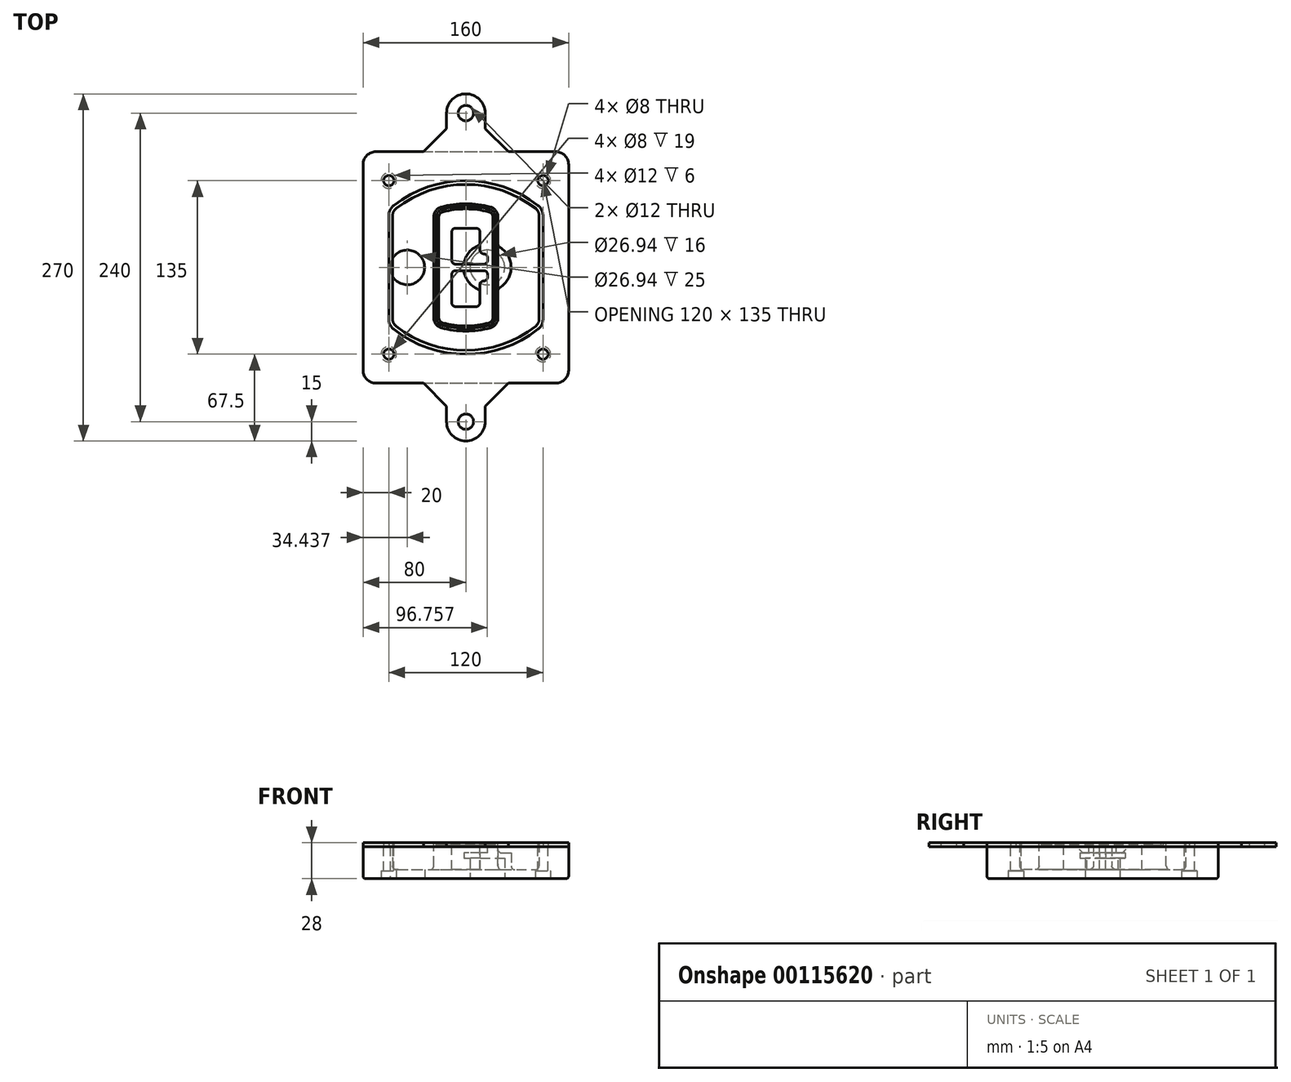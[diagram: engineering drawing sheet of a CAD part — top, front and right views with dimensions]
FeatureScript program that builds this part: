
annotation { "Feature Type Name" : "Feature", "Feature Type Description" : "" }
export const myFeature = defineFeature(function(context is Context, id is Id, definition is map)
    precondition{}
    {
        {
            var Q0;
            Q0=qCreatedBy(makeId("Top.planeOp"),FACE);
            var sketch = newSketch(context, id + "F0", { "sketchPlane" : qUnion([Q0])});
            skPoint(sketch, "E0.rect.middle", {"position": v(0, 0) * mm});
            skLineSegment(sketch, "E1.bottom", {"start": v(-70, -90) * mm, "end": v(70, -90) * mm});
            skLineSegment(sketch, "E1.top", {"start": v(-70, 90) * mm, "end": v(70, 90) * mm});
            skLineSegment(sketch, "E1.left", {"start": v(-80, -80) * mm, "end": v(-80, 80) * mm});
            skLineSegment(sketch, "E1.right", {"start": v(80, -80) * mm, "end": v(80, 80) * mm});
            skLineSegment(sketch, "E2", {"start": v(-80, 90) * mm, "end": v(80, -90) * mm, "construction": true});
            skLineSegment(sketch, "E3", {"start": v(80, 90) * mm, "end": v(-80, -90) * mm, "construction": true});
            skCircle(sketch, "E4", {"center": v(-60, 67.5) * mm, "radius": 4 * mm});
            skCircle(sketch, "E5", {"center": v(60, 67.5) * mm, "radius": 4 * mm});
            skCircle(sketch, "E6", {"center": v(60, -67.5) * mm, "radius": 4 * mm});
            skCircle(sketch, "E7", {"center": v(-60, -67.5) * mm, "radius": 4 * mm});
            skLineSegment(sketch, "E8", {"start": v(-60, 67.5) * mm, "end": v(60, 67.5) * mm, "construction": true});
            skLineSegment(sketch, "E9", {"start": v(60, 67.5) * mm, "end": v(60, -67.5) * mm, "construction": true});
            skLineSegment(sketch, "E10", {"start": v(60, -67.5) * mm, "end": v(-60, -67.5) * mm, "construction": true});
            skLineSegment(sketch, "E11", {"start": v(-60, -67.5) * mm, "end": v(-60, 67.5) * mm, "construction": true});
            skLineSegment(sketch, "E12", {"start": v(-60, 40.3) * mm, "end": v(-60, -40.3) * mm});
            skLineSegment(sketch, "E13", {"start": v(60, 40.3) * mm, "end": v(60, -40.3) * mm});
            skArc(sketch, "E14", {"start": v(56.15, 48.18) * mm, "mid": v(0, 67.5) * mm, "end": v(-56.15, 48.18) * mm});
            skArc(sketch, "E15", {"start": v(-56.15, -48.18) * mm, "mid": v(0, -67.5) * mm, "end": v(56.15, -48.18) * mm});
            skLineSegment(sketch, "E16", {"start": v(-60, 0) * mm, "end": v(60, 0) * mm, "construction": true});
            skPoint(sketch, "E17.visualSharp", {"position": v(-60, -45) * mm});
            skArc(sketch, "E17.filletArc", {"start": v(-60, -40.3) * mm, "mid": v(-58.99, -44.68) * mm, "end": v(-56.15, -48.18) * mm});
            skPoint(sketch, "E18.visualSharp", {"position": v(-60, 45) * mm});
            skArc(sketch, "E18.filletArc", {"start": v(-56.15, 48.18) * mm, "mid": v(-58.99, 44.68) * mm, "end": v(-60, 40.3) * mm});
            skPoint(sketch, "E19.visualSharp", {"position": v(60, 45) * mm});
            skArc(sketch, "E19.filletArc", {"start": v(60, 40.3) * mm, "mid": v(58.99, 44.68) * mm, "end": v(56.15, 48.18) * mm});
            skPoint(sketch, "E20.visualSharp", {"position": v(60, -45) * mm});
            skArc(sketch, "E20.filletArc", {"start": v(56.15, -48.18) * mm, "mid": v(58.99, -44.68) * mm, "end": v(60, -40.3) * mm});
            skPoint(sketch, "E21.visualSharp", {"position": v(-80, 90) * mm});
            skArc(sketch, "E21.filletArc", {"start": v(-70, 90) * mm, "mid": v(-77.07, 87.07) * mm, "end": v(-80, 80) * mm});
            skPoint(sketch, "E22.visualSharp", {"position": v(80, 90) * mm});
            skArc(sketch, "E22.filletArc", {"start": v(80, 80) * mm, "mid": v(77.07, 87.07) * mm, "end": v(70, 90) * mm});
            skPoint(sketch, "E23.visualSharp", {"position": v(80, -90) * mm});
            skArc(sketch, "E23.filletArc", {"start": v(70, -90) * mm, "mid": v(77.07, -87.07) * mm, "end": v(80, -80) * mm});
            skPoint(sketch, "E24.visualSharp", {"position": v(-80, -90) * mm});
            skArc(sketch, "E24.filletArc", {"start": v(-80, -80) * mm, "mid": v(-77.07, -87.07) * mm, "end": v(-70, -90) * mm});
            skArc(sketch, "E25.0", {"start": v(57, 40.3) * mm, "mid": v(56.3, 43.36) * mm, "end": v(54.3, 45.81) * mm});
            skLineSegment(sketch, "E25.1", {"start": v(57, 40.3) * mm, "end": v(57, -40.3) * mm});
            skArc(sketch, "E25.2", {"start": v(54.3, -45.81) * mm, "mid": v(56.3, -43.36) * mm, "end": v(57, -40.3) * mm});
            skArc(sketch, "E25.3", {"start": v(-54.3, -45.81) * mm, "mid": v(0, -64.5) * mm, "end": v(54.3, -45.81) * mm});
            skArc(sketch, "E25.4", {"start": v(-57, -40.3) * mm, "mid": v(-56.3, -43.36) * mm, "end": v(-54.3, -45.81) * mm});
            skArc(sketch, "E25.5", {"start": v(54.3, 45.81) * mm, "mid": v(0, 64.5) * mm, "end": v(-54.3, 45.81) * mm});
            skLineSegment(sketch, "E25.6", {"start": v(-57, 40.3) * mm, "end": v(-57, -40.3) * mm});
            skArc(sketch, "E25.7", {"start": v(-54.3, 45.81) * mm, "mid": v(-56.3, 43.36) * mm, "end": v(-57, 40.3) * mm});
            skArc(sketch, "E26.0", {"start": v(-58.62, 51.33) * mm, "mid": v(-62.58, 46.43) * mm, "end": v(-64, 40.3) * mm});
            skArc(sketch, "E26.1", {"start": v(58.62, 51.33) * mm, "mid": v(0, 71.5) * mm, "end": v(-58.62, 51.33) * mm});
            skArc(sketch, "E26.2", {"start": v(64, 40.3) * mm, "mid": v(62.58, 46.43) * mm, "end": v(58.62, 51.33) * mm});
            skLineSegment(sketch, "E26.3", {"start": v(64, 40.3) * mm, "end": v(64, -40.3) * mm});
            skArc(sketch, "E26.4", {"start": v(58.62, -51.33) * mm, "mid": v(62.58, -46.43) * mm, "end": v(64, -40.3) * mm});
            skLineSegment(sketch, "E26.5", {"start": v(-64, 40.3) * mm, "end": v(-64, -40.3) * mm});
            skArc(sketch, "E26.6", {"start": v(-58.62, -51.33) * mm, "mid": v(0, -71.5) * mm, "end": v(58.62, -51.33) * mm});
            skArc(sketch, "E26.7", {"start": v(-64, -40.3) * mm, "mid": v(-62.58, -46.43) * mm, "end": v(-58.62, -51.33) * mm});
            skSolve(sketch);
        }
        {
            var Q0;
            Q0=makeQuery(id+"F0.imprint","IMPRINT",FACE,{"disambiguationData":[TD([[makeQuery(id+"F0.imprint","IMPRINT",EDGE,{"derivedFrom":sQuery(id+"F0.wireOp",EDGE,"E1.bottom")}),1.0]])]});
            var Q1;
            Q1=makeQuery(id+"F0.imprint","IMPRINT",FACE,{"disambiguationData":[TD([[makeQuery(id+"F0.imprint","IMPRINT",EDGE,{"derivedFrom":sQuery(id+"F0.wireOp",EDGE,"E12")}),1.0]])]});
            var Q2;
            Q2=makeQuery(id+"F0.imprint","IMPRINT",FACE,{"disambiguationData":[TD([[makeQuery(id+"F0.imprint","IMPRINT",EDGE,{"derivedFrom":sQuery(id+"F0.wireOp",EDGE,"E25.0")}),1.0]])]});
            var Q3;
            Q3=makeQuery(id+"F0.imprint","IMPRINT",FACE,{"disambiguationData":[TD([[makeQuery(id+"F0.imprint","IMPRINT",EDGE,{"derivedFrom":sQuery(id+"F0.wireOp",EDGE,"E12")}),-1.0]])]});
            extrude(context, id + "F1", {"entities" : qUnion([Q0, Q1, Q2, Q3]), "oppositeDirection" : true, "depth" : 25 * mm});
        }
        {
            var Q0;
            Q0=makeQuery(id+"F0.imprint","IMPRINT",FACE,{"disambiguationData":[TD([[makeQuery(id+"F0.imprint","IMPRINT",EDGE,{"derivedFrom":sQuery(id+"F0.wireOp",EDGE,"E12")}),1.0]])]});
            extrude(context, id + "F2", {"entities" : qUnion([Q0]), "operationType" : NewBodyOperationType.ADD, "depth" : 3 * mm});
        }
        {
            var Q0;
            Q0=makeQuery(id+"F0.imprint","IMPRINT",FACE,{"disambiguationData":[TD([[makeQuery(id+"F0.imprint","IMPRINT",EDGE,{"derivedFrom":sQuery(id+"F0.wireOp",EDGE,"E25.0")}),1.0]])]});
            extrude(context, id + "F3", {"entities" : qUnion([Q0]), "operationType" : NewBodyOperationType.REMOVE, "oppositeDirection" : true, "depth" : 18 * mm});
        }
        {
            var Q0;
            Q0=makeQuery(id+"F2.opExtrude","CAP_FACE",FACE,{"disambiguationData":[OSD([sQuery(id+"F0.wireOp",EDGE,"E12"),sQuery(id+"F0.wireOp",EDGE,"E13"),sQuery(id+"F0.wireOp",EDGE,"E14"),sQuery(id+"F0.wireOp",EDGE,"E15"),sQuery(id+"F0.wireOp",EDGE,"E17.filletArc"),sQuery(id+"F0.wireOp",EDGE,"E18.filletArc"),sQuery(id+"F0.wireOp",EDGE,"E19.filletArc"),sQuery(id+"F0.wireOp",EDGE,"E20.filletArc"),sQuery(id+"F0.wireOp",EDGE,"E25.0"),sQuery(id+"F0.wireOp",EDGE,"E25.1"),sQuery(id+"F0.wireOp",EDGE,"E25.2"),sQuery(id+"F0.wireOp",EDGE,"E25.3"),sQuery(id+"F0.wireOp",EDGE,"E25.4"),sQuery(id+"F0.wireOp",EDGE,"E25.5"),sQuery(id+"F0.wireOp",EDGE,"E25.6"),sQuery(id+"F0.wireOp",EDGE,"E25.7")])],"isStart":false});
            var sketch = newSketch(context, id + "F4", { "sketchPlane" : qUnion([Q0])});
            skArc(sketch, "E27.0", {"start": v(-19.08, -46.97) * mm, "mid": v(0, -49.5) * mm, "end": v(19.08, -46.97) * mm});
            skArc(sketch, "E28.0", {"start": v(19.08, 46.97) * mm, "mid": v(0, 49.5) * mm, "end": v(-19.08, 46.97) * mm});
            skLineSegment(sketch, "E29", {"start": v(-25, 39.25) * mm, "end": v(-25, -39.25) * mm});
            skLineSegment(sketch, "E30", {"start": v(25, 39.25) * mm, "end": v(25, -39.25) * mm});
            skLineSegment(sketch, "E31", {"start": v(-25, 45.1) * mm, "end": v(25, 45.1) * mm, "construction": true});
            skLineSegment(sketch, "E32", {"start": v(-25, -45.1) * mm, "end": v(25, -45.1) * mm, "construction": true});
            skPoint(sketch, "E33.visualSharp", {"position": v(-25, 45.1) * mm});
            skArc(sketch, "E33.filletArc", {"start": v(-19.08, 46.97) * mm, "mid": v(-23.35, 44.11) * mm, "end": v(-25, 39.25) * mm});
            skPoint(sketch, "E34.visualSharp", {"position": v(25, 45.1) * mm});
            skArc(sketch, "E34.filletArc", {"start": v(25, 39.25) * mm, "mid": v(23.35, 44.11) * mm, "end": v(19.08, 46.97) * mm});
            skPoint(sketch, "E35.visualSharp", {"position": v(25, -45.1) * mm});
            skArc(sketch, "E35.filletArc", {"start": v(19.08, -46.97) * mm, "mid": v(23.35, -44.11) * mm, "end": v(25, -39.25) * mm});
            skPoint(sketch, "E36.visualSharp", {"position": v(-25, -45.1) * mm});
            skArc(sketch, "E36.filletArc", {"start": v(-25, -39.25) * mm, "mid": v(-23.35, -44.11) * mm, "end": v(-19.08, -46.97) * mm});
            skArc(sketch, "E37.0", {"start": v(54.3, 45.81) * mm, "mid": v(0, 64.5) * mm, "end": v(-54.3, 45.81) * mm});
            skArc(sketch, "E37.1", {"start": v(-54.3, 45.81) * mm, "mid": v(-56.3, 43.36) * mm, "end": v(-57, 40.3) * mm});
            skLineSegment(sketch, "E37.2", {"start": v(-57, 40.3) * mm, "end": v(-57, -40.3) * mm});
            skArc(sketch, "E37.3", {"start": v(-57, -40.3) * mm, "mid": v(-56.3, -43.36) * mm, "end": v(-54.3, -45.81) * mm});
            skArc(sketch, "E37.4", {"start": v(-54.3, -45.81) * mm, "mid": v(0, -64.5) * mm, "end": v(54.3, -45.81) * mm});
            skArc(sketch, "E37.5", {"start": v(54.3, -45.81) * mm, "mid": v(56.3, -43.36) * mm, "end": v(57, -40.3) * mm});
            skLineSegment(sketch, "E37.6", {"start": v(57, 40.3) * mm, "end": v(57, -40.3) * mm});
            skArc(sketch, "E37.7", {"start": v(57, 40.3) * mm, "mid": v(56.3, 43.36) * mm, "end": v(54.3, 45.81) * mm});
            skLineSegment(sketch, "E38.0", {"start": v(23, 39.25) * mm, "end": v(23, -39.25) * mm});
            skArc(sketch, "E38.1", {"start": v(18.56, -45.04) * mm, "mid": v(21.76, -42.9) * mm, "end": v(23, -39.25) * mm});
            skArc(sketch, "E38.2", {"start": v(-18.56, -45.04) * mm, "mid": v(0, -47.5) * mm, "end": v(18.56, -45.04) * mm});
            skArc(sketch, "E38.3", {"start": v(-23, -39.25) * mm, "mid": v(-21.76, -42.9) * mm, "end": v(-18.56, -45.04) * mm});
            skLineSegment(sketch, "E38.4", {"start": v(-23, 39.25) * mm, "end": v(-23, -39.25) * mm});
            skArc(sketch, "E38.5", {"start": v(23, 39.25) * mm, "mid": v(21.76, 42.9) * mm, "end": v(18.56, 45.04) * mm});
            skArc(sketch, "E38.6", {"start": v(-18.56, 45.04) * mm, "mid": v(-21.76, 42.9) * mm, "end": v(-23, 39.25) * mm});
            skArc(sketch, "E38.7", {"start": v(18.56, 45.04) * mm, "mid": v(0, 47.5) * mm, "end": v(-18.56, 45.04) * mm});
            skArc(sketch, "E39.0", {"start": v(21, 39.25) * mm, "mid": v(20.18, 41.68) * mm, "end": v(18.04, 43.1) * mm});
            skLineSegment(sketch, "E39.1", {"start": v(21, 39.25) * mm, "end": v(21, -39.25) * mm});
            skArc(sketch, "E39.2", {"start": v(18.04, -43.1) * mm, "mid": v(20.18, -41.68) * mm, "end": v(21, -39.25) * mm});
            skArc(sketch, "E39.3", {"start": v(-18.04, -43.1) * mm, "mid": v(0, -45.5) * mm, "end": v(18.04, -43.1) * mm});
            skArc(sketch, "E39.4", {"start": v(-21, -39.25) * mm, "mid": v(-20.18, -41.68) * mm, "end": v(-18.04, -43.1) * mm});
            skArc(sketch, "E39.5", {"start": v(18.04, 43.1) * mm, "mid": v(0, 45.5) * mm, "end": v(-18.04, 43.1) * mm});
            skLineSegment(sketch, "E39.6", {"start": v(-21, 39.25) * mm, "end": v(-21, -39.25) * mm});
            skArc(sketch, "E39.7", {"start": v(-18.04, 43.1) * mm, "mid": v(-20.18, 41.68) * mm, "end": v(-21, 39.25) * mm});
            skLineSegment(sketch, "E40", {"start": v(-25, 0) * mm, "end": v(25, 0) * mm, "construction": true});
            skLineSegment(sketch, "E41", {"start": v(-11, 5.5) * mm, "end": v(-11, 27.5) * mm});
            skLineSegment(sketch, "E42", {"start": v(-8, 30.5) * mm, "end": v(8, 30.5) * mm});
            skLineSegment(sketch, "E43", {"start": v(11, 27.5) * mm, "end": v(11, 13.5) * mm});
            skLineSegment(sketch, "E44", {"start": v(14, 10.5) * mm, "end": v(14, 10.5) * mm});
            skLineSegment(sketch, "E45", {"start": v(17, 7.5) * mm, "end": v(17, 5.5) * mm});
            skLineSegment(sketch, "E46", {"start": v(14, 2.5) * mm, "end": v(-8, 2.5) * mm});
            skPoint(sketch, "E47.visualSharp", {"position": v(-11, 30.5) * mm});
            skArc(sketch, "E47.filletArc", {"start": v(-8, 30.5) * mm, "mid": v(-10.12, 29.62) * mm, "end": v(-11, 27.5) * mm});
            skPoint(sketch, "E48.visualSharp", {"position": v(11, 30.5) * mm});
            skArc(sketch, "E48.filletArc", {"start": v(11, 27.5) * mm, "mid": v(10.12, 29.62) * mm, "end": v(8, 30.5) * mm});
            skPoint(sketch, "E49.visualSharp", {"position": v(11, 10.5) * mm});
            skArc(sketch, "E49.filletArc", {"start": v(11, 13.5) * mm, "mid": v(11.88, 11.38) * mm, "end": v(14, 10.5) * mm});
            skPoint(sketch, "E50.visualSharp", {"position": v(17, 10.5) * mm});
            skArc(sketch, "E50.filletArc", {"start": v(17, 7.5) * mm, "mid": v(16.12, 9.62) * mm, "end": v(14, 10.5) * mm});
            skPoint(sketch, "E51.visualSharp", {"position": v(17, 2.5) * mm});
            skArc(sketch, "E51.filletArc", {"start": v(14, 2.5) * mm, "mid": v(16.12, 3.38) * mm, "end": v(17, 5.5) * mm});
            skPoint(sketch, "E52.visualSharp", {"position": v(-11, 2.5) * mm});
            skArc(sketch, "E52.filletArc", {"start": v(-11, 5.5) * mm, "mid": v(-10.12, 3.38) * mm, "end": v(-8, 2.5) * mm});
            skLineSegment(sketch, "E53.0.MirrorCS", {"start": v(14, -2.5) * mm, "end": v(-8, -2.5) * mm});
            skArc(sketch, "E54.0.MirrorCS", {"start": v(-11, -5.5) * mm, "mid": v(-10.12, -3.38) * mm, "end": v(-8, -2.5) * mm});
            skLineSegment(sketch, "E55.0.MirrorCS", {"start": v(-11, -5.5) * mm, "end": v(-11, -27.5) * mm});
            skArc(sketch, "E56.0.MirrorCS", {"start": v(-8, -30.5) * mm, "mid": v(-10.12, -29.62) * mm, "end": v(-11, -27.5) * mm});
            skLineSegment(sketch, "E57.0.MirrorCS", {"start": v(-8, -30.5) * mm, "end": v(8, -30.5) * mm});
            skArc(sketch, "E58.0.MirrorCS", {"start": v(11, -27.5) * mm, "mid": v(10.12, -29.62) * mm, "end": v(8, -30.5) * mm});
            skLineSegment(sketch, "E59.0.MirrorCS", {"start": v(11, -27.5) * mm, "end": v(11, -13.5) * mm});
            skArc(sketch, "E60.0.MirrorCS", {"start": v(11, -13.5) * mm, "mid": v(11.88, -11.38) * mm, "end": v(14, -10.5) * mm});
            skArc(sketch, "E61.0.MirrorCS", {"start": v(17, -7.5) * mm, "mid": v(16.12, -9.62) * mm, "end": v(14, -10.5) * mm});
            skLineSegment(sketch, "E62.0.MirrorCS", {"start": v(17, -7.5) * mm, "end": v(17, -5.5) * mm});
            skArc(sketch, "E63.0.MirrorCS", {"start": v(14, -2.5) * mm, "mid": v(16.12, -3.38) * mm, "end": v(17, -5.5) * mm});
            skSolve(sketch);
        }
        {
            var Q0;
            Q0=makeQuery(id+"F4.imprint","IMPRINT",FACE,{"disambiguationData":[TD([[makeQuery(id+"F4.imprint","IMPRINT",EDGE,{"derivedFrom":sQuery(id+"F4.wireOp",EDGE,"E27.0")}),1.0]])]});
            var Q1;
            Q1=makeQuery(id+"F4.imprint","IMPRINT",FACE,{"disambiguationData":[TD([[makeQuery(id+"F4.imprint","IMPRINT",EDGE,{"derivedFrom":sQuery(id+"F4.wireOp",EDGE,"E38.0")}),-1.0]])]});
            var Q2;
            Q2=makeQuery(id+"F4.imprint","IMPRINT",FACE,{"disambiguationData":[TD([[makeQuery(id+"F4.imprint","IMPRINT",EDGE,{"derivedFrom":sQuery(id+"F4.wireOp",EDGE,"E39.0")}),1.0]])]});
            extrude(context, id + "F5", {"entities" : qUnion([Q0, Q1, Q2]), "operationType" : NewBodyOperationType.ADD, "endBound" : BoundingType.UP_TO_NEXT, "oppositeDirection" : true, "depth" : 25 * mm});
        }
        {
            var Q0;
            Q0=makeQuery(id+"F4.imprint","IMPRINT",FACE,{"disambiguationData":[TD([[makeQuery(id+"F4.imprint","IMPRINT",EDGE,{"derivedFrom":sQuery(id+"F4.wireOp",EDGE,"E38.0")}),-1.0]])]});
            extrude(context, id + "F6", {"entities" : qUnion([Q0]), "operationType" : NewBodyOperationType.REMOVE, "oppositeDirection" : true, "depth" : 2 * mm});
        }
        {
            var Q0;
            Q0=makeQuery(id+"F1.opExtrude","CAP_FACE",FACE,{"disambiguationData":[OSD([sQuery(id+"F0.wireOp",EDGE,"E1.bottom"),sQuery(id+"F0.wireOp",EDGE,"E1.top"),sQuery(id+"F0.wireOp",EDGE,"E1.left"),sQuery(id+"F0.wireOp",EDGE,"E1.right"),sQuery(id+"F0.wireOp",EDGE,"E4"),sQuery(id+"F0.wireOp",EDGE,"E5"),sQuery(id+"F0.wireOp",EDGE,"E6"),sQuery(id+"F0.wireOp",EDGE,"E7"),sQuery(id+"F0.wireOp",EDGE,"E21.filletArc"),sQuery(id+"F0.wireOp",EDGE,"E22.filletArc"),sQuery(id+"F0.wireOp",EDGE,"E23.filletArc"),sQuery(id+"F0.wireOp",EDGE,"E24.filletArc")])],"isStart":false});
            var sketch = newSketch(context, id + "F7", { "sketchPlane" : qUnion([Q0])});
            skCircle(sketch, "E64", {"center": v(16.76, 0) * mm, "radius": 13.47 * mm});
            skCircle(sketch, "E65", {"center": v(-45.56, 0) * mm, "radius": 13.47 * mm});
            skLineSegment(sketch, "E66", {"start": v(80, 0) * mm, "end": v(-80, 0) * mm});
            skCircle(sketch, "E67", {"center": v(16.76, 0) * mm, "radius": 18.47 * mm});
            skCircle(sketch, "E68", {"center": v(60, -67.5) * mm, "radius": 6 * mm});
            skCircle(sketch, "E69", {"center": v(-60, -67.5) * mm, "radius": 6 * mm});
            skCircle(sketch, "E70", {"center": v(-60, 67.5) * mm, "radius": 6 * mm});
            skCircle(sketch, "E71", {"center": v(60, 67.5) * mm, "radius": 6 * mm});
            skSolve(sketch);
        }
        {
            var Q0;
            {var subQ1=sQuery(id+"F7.wireOp",EDGE,"E66");var subQ4=sQuery(id+"F7.wireOp",EDGE,"E64");var subQ6=makeQuery(id+"F7.imprint","INTERSECT",VERTEX,{"disambiguationData":[OD(0.0)],"derivedFrom":[subQ4,subQ1]});Q0=makeQuery(id+"F7.imprint","IMPRINT",FACE,{"disambiguationData":[TD([[makeQuery(id+"F7.imprint","IMPRINT",EDGE,{"disambiguationData":[TD([[subQ6,-1.0]])],"derivedFrom":subQ4}),-1.0]])]});}
            var Q1;
            {var subQ0=sQuery(id+"F7.wireOp",EDGE,"E66");var subQ1=sQuery(id+"F7.wireOp",EDGE,"E64");var subQ3=makeQuery(id+"F7.imprint","INTERSECT",VERTEX,{"disambiguationData":[OD(0.0)],"derivedFrom":[subQ1,subQ0]});Q1=makeQuery(id+"F7.imprint","IMPRINT",FACE,{"disambiguationData":[TD([[makeQuery(id+"F7.imprint","IMPRINT",EDGE,{"disambiguationData":[TD([[subQ3,-1.0]])],"derivedFrom":subQ1}),1.0]])]});}
            var Q2;
            {var subQ0=sQuery(id+"F7.wireOp",EDGE,"E66");var subQ1=sQuery(id+"F7.wireOp",EDGE,"E64");var subQ3=makeQuery(id+"F7.imprint","INTERSECT",VERTEX,{"disambiguationData":[OD(0.0)],"derivedFrom":[subQ1,subQ0]});Q2=makeQuery(id+"F7.imprint","IMPRINT",FACE,{"disambiguationData":[TD([[makeQuery(id+"F7.imprint","IMPRINT",EDGE,{"disambiguationData":[TD([[subQ3,1.0]])],"derivedFrom":subQ1}),1.0]])]});}
            var Q3;
            {var subQ1=sQuery(id+"F7.wireOp",EDGE,"E66");var subQ4=sQuery(id+"F7.wireOp",EDGE,"E64");var subQ6=makeQuery(id+"F7.imprint","INTERSECT",VERTEX,{"disambiguationData":[OD(0.0)],"derivedFrom":[subQ4,subQ1]});Q3=makeQuery(id+"F7.imprint","IMPRINT",FACE,{"disambiguationData":[TD([[makeQuery(id+"F7.imprint","IMPRINT",EDGE,{"disambiguationData":[TD([[subQ6,1.0]])],"derivedFrom":subQ4}),-1.0]])]});}
            extrude(context, id + "F8", {"entities" : qUnion([Q0, Q1, Q2, Q3]), "operationType" : NewBodyOperationType.ADD, "oppositeDirection" : true, "depth" : 20 * mm});
        }
        {
            var Q0;
            {var subQ0=sQuery(id+"F7.wireOp",EDGE,"E66");var subQ1=sQuery(id+"F7.wireOp",EDGE,"E64");var subQ3=makeQuery(id+"F7.imprint","INTERSECT",VERTEX,{"disambiguationData":[OD(0.0)],"derivedFrom":[subQ1,subQ0]});Q0=makeQuery(id+"F7.imprint","IMPRINT",FACE,{"disambiguationData":[TD([[makeQuery(id+"F7.imprint","IMPRINT",EDGE,{"disambiguationData":[TD([[subQ3,-1.0]])],"derivedFrom":subQ1}),1.0]])]});}
            var Q1;
            {var subQ0=sQuery(id+"F7.wireOp",EDGE,"E66");var subQ1=sQuery(id+"F7.wireOp",EDGE,"E64");var subQ3=makeQuery(id+"F7.imprint","INTERSECT",VERTEX,{"disambiguationData":[OD(0.0)],"derivedFrom":[subQ1,subQ0]});Q1=makeQuery(id+"F7.imprint","IMPRINT",FACE,{"disambiguationData":[TD([[makeQuery(id+"F7.imprint","IMPRINT",EDGE,{"disambiguationData":[TD([[subQ3,1.0]])],"derivedFrom":subQ1}),1.0]])]});}
            extrude(context, id + "F9", {"entities" : qUnion([Q0, Q1]), "operationType" : NewBodyOperationType.REMOVE, "oppositeDirection" : true, "depth" : 16 * mm});
        }
        {
            var Q0;
            {var subQ0=sQuery(id+"F7.wireOp",EDGE,"E66");var subQ1=sQuery(id+"F7.wireOp",EDGE,"E65");var subQ3=makeQuery(id+"F7.imprint","INTERSECT",VERTEX,{"disambiguationData":[OD(0.0)],"derivedFrom":[subQ1,subQ0]});Q0=makeQuery(id+"F7.imprint","IMPRINT",FACE,{"disambiguationData":[TD([[makeQuery(id+"F7.imprint","IMPRINT",EDGE,{"disambiguationData":[TD([[subQ3,-1.0]])],"derivedFrom":subQ1}),1.0]])]});}
            var Q1;
            {var subQ0=sQuery(id+"F7.wireOp",EDGE,"E66");var subQ1=sQuery(id+"F7.wireOp",EDGE,"E65");var subQ3=makeQuery(id+"F7.imprint","INTERSECT",VERTEX,{"disambiguationData":[OD(0.0)],"derivedFrom":[subQ1,subQ0]});Q1=makeQuery(id+"F7.imprint","IMPRINT",FACE,{"disambiguationData":[TD([[makeQuery(id+"F7.imprint","IMPRINT",EDGE,{"disambiguationData":[TD([[subQ3,1.0]])],"derivedFrom":subQ1}),1.0]])]});}
            extrude(context, id + "F10", {"entities" : qUnion([Q0, Q1]), "operationType" : NewBodyOperationType.REMOVE, "oppositeDirection" : true, "depth" : 25 * mm});
        }
        {
            var Q0;
            Q0=makeQuery(id+"F7.imprint","IMPRINT",FACE,{"disambiguationData":[TD([[makeQuery(id+"F7.imprint","IMPRINT",EDGE,{"derivedFrom":sQuery(id+"F7.wireOp",EDGE,"E68")}),1.0]])]});
            var Q1;
            Q1=makeQuery(id+"F7.imprint","IMPRINT",FACE,{"disambiguationData":[TD([[makeQuery(id+"F7.imprint","IMPRINT",EDGE,{"derivedFrom":makeQuery(id+"F1.opExtrude","CAP_EDGE",EDGE,{"disambiguationData":[OSD([sQuery(id+"F0.wireOp",EDGE,"E5")])],"isStart":false})}),-1.0]])]});
            var Q2;
            Q2=makeQuery(id+"F7.imprint","IMPRINT",FACE,{"disambiguationData":[TD([[makeQuery(id+"F7.imprint","IMPRINT",EDGE,{"derivedFrom":sQuery(id+"F7.wireOp",EDGE,"E69")}),1.0]])]});
            var Q3;
            Q3=makeQuery(id+"F7.imprint","IMPRINT",FACE,{"disambiguationData":[TD([[makeQuery(id+"F7.imprint","IMPRINT",EDGE,{"derivedFrom":makeQuery(id+"F1.opExtrude","CAP_EDGE",EDGE,{"disambiguationData":[OSD([sQuery(id+"F0.wireOp",EDGE,"E4")])],"isStart":false})}),-1.0]])]});
            var Q4;
            Q4=makeQuery(id+"F7.imprint","IMPRINT",FACE,{"disambiguationData":[TD([[makeQuery(id+"F7.imprint","IMPRINT",EDGE,{"derivedFrom":sQuery(id+"F7.wireOp",EDGE,"E70")}),1.0]])]});
            var Q5;
            Q5=makeQuery(id+"F7.imprint","IMPRINT",FACE,{"disambiguationData":[TD([[makeQuery(id+"F7.imprint","IMPRINT",EDGE,{"derivedFrom":makeQuery(id+"F1.opExtrude","CAP_EDGE",EDGE,{"disambiguationData":[OSD([sQuery(id+"F0.wireOp",EDGE,"E7")])],"isStart":false})}),-1.0]])]});
            var Q6;
            Q6=makeQuery(id+"F7.imprint","IMPRINT",FACE,{"disambiguationData":[TD([[makeQuery(id+"F7.imprint","IMPRINT",EDGE,{"derivedFrom":sQuery(id+"F7.wireOp",EDGE,"E71")}),1.0]])]});
            var Q7;
            Q7=makeQuery(id+"F7.imprint","IMPRINT",FACE,{"disambiguationData":[TD([[makeQuery(id+"F7.imprint","IMPRINT",EDGE,{"derivedFrom":makeQuery(id+"F1.opExtrude","CAP_EDGE",EDGE,{"disambiguationData":[OSD([sQuery(id+"F0.wireOp",EDGE,"E6")])],"isStart":false})}),-1.0]])]});
            extrude(context, id + "F11", {"entities" : qUnion([Q0, Q1, Q2, Q3, Q4, Q5, Q6, Q7]), "operationType" : NewBodyOperationType.REMOVE, "oppositeDirection" : true, "depth" : 6 * mm});
        }
        {
            var Q0;
            Q0=makeQuery(id+"F9.boolean.opBoolean","COPY",FACE,{"derivedFrom":makeQuery(id+"F9.opExtrude","CAP_FACE",FACE,{"disambiguationData":[OSD([sQuery(id+"F7.wireOp",EDGE,"E64")])],"isStart":false})});
            var sketch = newSketch(context, id + "F12", { "sketchPlane" : qUnion([Q0])});
            skArc(sketch, "E72.0", {"start": v(11, 17.55) * mm, "mid": v(2.57, 11.82) * mm, "end": v(-1.54, 2.5) * mm});
            skArc(sketch, "E72.1", {"start": v(-1.54, -2.5) * mm, "mid": v(2.57, -11.82) * mm, "end": v(11, -17.55) * mm});
            skLineSegment(sketch, "E73", {"start": v(-1.54, -2.5) * mm, "end": v(14, -2.5) * mm});
            skLineSegment(sketch, "E74.0", {"start": v(14, 2.5) * mm, "end": v(-1.54, 2.5) * mm});
            skArc(sketch, "E74.1", {"start": v(14, 2.5) * mm, "mid": v(16.12, 3.38) * mm, "end": v(17, 5.5) * mm});
            skLineSegment(sketch, "E74.2", {"start": v(17, 7.5) * mm, "end": v(17, 5.5) * mm});
            skArc(sketch, "E74.3", {"start": v(17, 7.5) * mm, "mid": v(16.12, 9.62) * mm, "end": v(14, 10.5) * mm});
            skArc(sketch, "E74.4", {"start": v(11, 13.5) * mm, "mid": v(11.88, 11.38) * mm, "end": v(14, 10.5) * mm});
            skLineSegment(sketch, "E74.5", {"start": v(11, 17.55) * mm, "end": v(11, 13.5) * mm});
            skLineSegment(sketch, "E74.7", {"start": v(14, -2.5) * mm, "end": v(-1.54, -2.5) * mm});
            skArc(sketch, "E74.8", {"start": v(14, -2.5) * mm, "mid": v(16.12, -3.38) * mm, "end": v(17, -5.5) * mm});
            skLineSegment(sketch, "E74.9", {"start": v(17, -7.5) * mm, "end": v(17, -5.5) * mm});
            skArc(sketch, "E74.10", {"start": v(17, -7.5) * mm, "mid": v(16.12, -9.62) * mm, "end": v(14, -10.5) * mm});
            skArc(sketch, "E74.11", {"start": v(11, -13.5) * mm, "mid": v(11.88, -11.38) * mm, "end": v(14, -10.5) * mm});
            skLineSegment(sketch, "E74.12", {"start": v(11, -17.55) * mm, "end": v(11, -13.5) * mm});
            skPoint(sketch, "E75.orphan", {"position": v(11, -27.5) * mm});
            skPoint(sketch, "E76.orphan", {"position": v(-8, -2.5) * mm});
            skPoint(sketch, "E77.orphan", {"position": v(-8, 2.5) * mm});
            skPoint(sketch, "E78.orphan", {"position": v(11, 27.5) * mm});
            skSolve(sketch);
        }
        {
            var Q0;
            {var subQ7=sQuery(id+"F12.wireOp",EDGE,"E72.0");var subQ14=sQuery(id+"F12.wireOp",EDGE,"E72.1");var subQ16=sQuery(id+"F12.wireOp",EDGE,"E74.1");var subQ18=sQuery(id+"F12.wireOp",EDGE,"E74.8");Q0=qUnion([makeQuery(id+"F12.imprint","IMPRINT",FACE,{"disambiguationData":[TD([[makeQuery(id+"F12.imprint","IMPRINT",EDGE,{"derivedFrom":subQ7}),1.0]])]}),makeQuery(id+"F12.imprint","IMPRINT",FACE,{"disambiguationData":[TD([[makeQuery(id+"F12.imprint","IMPRINT",EDGE,{"derivedFrom":subQ14}),1.0]])]}),makeQuery(id+"F12.imprint","IMPRINT",FACE,{"disambiguationData":[TD([[makeQuery(id+"F12.imprint","IMPRINT",EDGE,{"derivedFrom":subQ16}),1.0]])]}),makeQuery(id+"F12.imprint","IMPRINT",FACE,{"disambiguationData":[TD([[makeQuery(id+"F12.imprint","IMPRINT",EDGE,{"derivedFrom":subQ18}),-1.0]])]})]);}
            var Q1;
            Q1=makeQuery(id+"F5.boolean.opBoolean","SPLIT",FACE,{"disambiguationData":[TD([makeQuery(id+"F5.opExtrude","SWEPT_FACE",FACE,{"disambiguationData":[OSD([sQuery(id+"F4.wireOp",EDGE,"E41")])]})])],"derivedFrom":makeQuery(id+"F3.boolean.opBoolean","COPY",FACE,{"derivedFrom":makeQuery(id+"F3.opExtrude","CAP_FACE",FACE,{"disambiguationData":[OSD([sQuery(id+"F0.wireOp",EDGE,"E25.0"),sQuery(id+"F0.wireOp",EDGE,"E25.1"),sQuery(id+"F0.wireOp",EDGE,"E25.2"),sQuery(id+"F0.wireOp",EDGE,"E25.3"),sQuery(id+"F0.wireOp",EDGE,"E25.4"),sQuery(id+"F0.wireOp",EDGE,"E25.5"),sQuery(id+"F0.wireOp",EDGE,"E25.6"),sQuery(id+"F0.wireOp",EDGE,"E25.7")])],"isStart":false})})});
            extrude(context, id + "F13", {"entities" : qUnion([Q0]), "operationType" : NewBodyOperationType.REMOVE, "endBound" : BoundingType.UP_TO_SURFACE, "endBoundEntityFace" : qUnion([Q1]), "depth" : 25 * mm});
        }
        {
            var Q0;
            Q0=makeQuery(id+"F3.boolean.opBoolean","COPY",EDGE,{"derivedFrom":makeQuery(id+"F3.opExtrude","CAP_EDGE",EDGE,{"disambiguationData":[OSD([sQuery(id+"F0.wireOp",EDGE,"E25.6")])],"isStart":false})});
            var Q1;
            Q1=makeQuery(id+"F8.boolean.opBoolean","INTERSECT",EDGE,{"derivedFrom":[makeQuery(id+"F5.opExtrude","SWEPT_FACE",FACE,{"disambiguationData":[OSD([sQuery(id+"F4.wireOp",EDGE,"E30")])]}),makeQuery(id+"F8.opExtrude","CAP_FACE",FACE,{"disambiguationData":[OSD([sQuery(id+"F7.wireOp",EDGE,"E67")])],"isStart":false})]});
            var Q2;
            Q2=makeQuery(id+"F8.boolean.opBoolean","INTERSECT",EDGE,{"disambiguationData":[OD(1.0)],"derivedFrom":[makeQuery(id+"F5.opExtrude","SWEPT_FACE",FACE,{"disambiguationData":[OSD([sQuery(id+"F4.wireOp",EDGE,"E30")])]}),makeQuery(id+"F8.opExtrude","SWEPT_FACE",FACE,{"disambiguationData":[OSD([sQuery(id+"F7.wireOp",EDGE,"E67")])]})]});
            var Q3;
            {var subQ0=sQuery(id+"F4.wireOp",EDGE,"E30");Q3=makeQuery(id+"F8.boolean.opBoolean","SPLIT",EDGE,{"disambiguationData":[TD([makeQuery(id+"F5.opExtrude","SWEPT_FACE",FACE,{"disambiguationData":[OSD([sQuery(id+"F4.wireOp",EDGE,"E35.filletArc")])]})])],"derivedFrom":makeQuery(id+"F5.opExtrude","CAP_EDGE",EDGE,{"disambiguationData":[OSD([subQ0])],"isStart":false})});}
            var Q4;
            {var subQ0=sQuery(id+"F0.wireOp",EDGE,"E25.7");var subQ1=sQuery(id+"F0.wireOp",EDGE,"E25.1");var subQ2=sQuery(id+"F0.wireOp",EDGE,"E25.6");var subQ3=sQuery(id+"F0.wireOp",EDGE,"E25.5");var subQ4=sQuery(id+"F0.wireOp",EDGE,"E25.4");var subQ5=sQuery(id+"F0.wireOp",EDGE,"E25.0");var subQ6=sQuery(id+"F0.wireOp",EDGE,"E25.2");var subQ7=sQuery(id+"F0.wireOp",EDGE,"E25.3");Q4=makeQuery(id+"F8.boolean.opBoolean","INTERSECT",EDGE,{"derivedFrom":[makeQuery(id+"F5.boolean.opBoolean","SPLIT",FACE,{"disambiguationData":[TD([makeQuery(id+"F2.opExtrude","SWEPT_FACE",FACE,{"disambiguationData":[OSD([subQ5])]})])],"derivedFrom":makeQuery(id+"F3.boolean.opBoolean","COPY",FACE,{"derivedFrom":makeQuery(id+"F3.opExtrude","CAP_FACE",FACE,{"disambiguationData":[OSD([subQ5,subQ1,subQ6,subQ7,subQ4,subQ3,subQ2,subQ0])],"isStart":false})})}),makeQuery(id+"F8.opExtrude","SWEPT_FACE",FACE,{"disambiguationData":[OSD([sQuery(id+"F7.wireOp",EDGE,"E67")])]})]});}
            var Q5;
            Q5=makeQuery(id+"F8.boolean.opBoolean","INTERSECT",EDGE,{"disambiguationData":[OD(0.0)],"derivedFrom":[makeQuery(id+"F5.opExtrude","SWEPT_FACE",FACE,{"disambiguationData":[OSD([sQuery(id+"F4.wireOp",EDGE,"E30")])]}),makeQuery(id+"F8.opExtrude","SWEPT_FACE",FACE,{"disambiguationData":[OSD([sQuery(id+"F7.wireOp",EDGE,"E67")])]})]});
            fillet(context, id + "F14", {"entities" : qUnion([Q0, Q1, Q2, Q3, Q4, Q5]), "radius" : 3 * mm, "tangentPropagation" : true, "allowEdgeOverflow" : false});
        }
        {
            var Q0;
            Q0=makeQuery(id+"F1.opExtrude","CAP_EDGE",EDGE,{"disambiguationData":[OSD([sQuery(id+"F0.wireOp",EDGE,"E1.bottom")])],"isStart":false});
            fillet(context, id + "F15", {"entities" : qUnion([Q0]), "radius" : 2 * mm, "tangentPropagation" : true, "allowEdgeOverflow" : false});
        }
        {
            var Q0;
            {var subQ0=sQuery(id+"F0.wireOp",EDGE,"E22.filletArc");var subQ1=sQuery(id+"F0.wireOp",EDGE,"E7");var subQ2=sQuery(id+"F0.wireOp",EDGE,"E6");var subQ3=sQuery(id+"F0.wireOp",EDGE,"E5");var subQ4=sQuery(id+"F0.wireOp",EDGE,"E4");var subQ5=sQuery(id+"F0.wireOp",EDGE,"E1.bottom");var subQ6=sQuery(id+"F0.wireOp",EDGE,"E21.filletArc");var subQ7=sQuery(id+"F0.wireOp",EDGE,"E1.top");var subQ8=sQuery(id+"F0.wireOp",EDGE,"E1.left");var subQ9=sQuery(id+"F0.wireOp",EDGE,"E1.right");var subQ10=sQuery(id+"F0.wireOp",EDGE,"E23.filletArc");var subQ11=sQuery(id+"F0.wireOp",EDGE,"E24.filletArc");Q0=makeQuery(id+"F2.boolean.opBoolean","SPLIT",FACE,{"disambiguationData":[TD([makeQuery(id+"F1.opExtrude","SWEPT_FACE",FACE,{"disambiguationData":[OSD([subQ5])]})])],"derivedFrom":makeQuery(id+"F1.opExtrude","CAP_FACE",FACE,{"disambiguationData":[OSD([subQ5,subQ7,subQ8,subQ9,subQ4,subQ3,subQ2,subQ1,subQ6,subQ0,subQ10,subQ11])],"isStart":true})});}
            var sketch = newSketch(context, id + "F16", { "sketchPlane" : qUnion([Q0])});
            skLineSegment(sketch, "E79.0", {"start": v(-80, -80) * mm, "end": v(-80, 80) * mm});
            skArc(sketch, "E79.1", {"start": v(-70, 90) * mm, "mid": v(-77.07, 87.07) * mm, "end": v(-80, 80) * mm});
            skLineSegment(sketch, "E79.2", {"start": v(-70, 90) * mm, "end": v(70, 90) * mm});
            skArc(sketch, "E79.3", {"start": v(80, 80) * mm, "mid": v(77.07, 87.07) * mm, "end": v(70, 90) * mm});
            skLineSegment(sketch, "E79.4", {"start": v(80, -80) * mm, "end": v(80, 80) * mm});
            skArc(sketch, "E79.5", {"start": v(70, -90) * mm, "mid": v(77.07, -87.07) * mm, "end": v(80, -80) * mm});
            skLineSegment(sketch, "E79.6", {"start": v(-70, -90) * mm, "end": v(70, -90) * mm});
            skArc(sketch, "E79.7", {"start": v(-80, -80) * mm, "mid": v(-77.07, -87.07) * mm, "end": v(-70, -90) * mm});
            skCircle(sketch, "E79.8", {"center": v(-60, -67.5) * mm, "radius": 4 * mm});
            skCircle(sketch, "E79.9", {"center": v(-60, 67.5) * mm, "radius": 4 * mm});
            skCircle(sketch, "E79.10", {"center": v(60, 67.5) * mm, "radius": 4 * mm});
            skCircle(sketch, "E79.11", {"center": v(60, -67.5) * mm, "radius": 4 * mm});
            skLineSegment(sketch, "E80", {"start": v(-33, 90) * mm, "end": v(-15, 108) * mm});
            skLineSegment(sketch, "E81", {"start": v(-15, 108) * mm, "end": v(-15, 120) * mm});
            skArc(sketch, "E82", {"start": v(15, 120) * mm, "mid": v(0, 135) * mm, "end": v(-15, 120) * mm});
            skLineSegment(sketch, "E83", {"start": v(15, 120) * mm, "end": v(15, 108) * mm});
            skLineSegment(sketch, "E84", {"start": v(15, 108) * mm, "end": v(33, 90) * mm});
            skLineSegment(sketch, "E85", {"start": v(0, 90) * mm, "end": v(0, 120) * mm, "construction": true});
            skCircle(sketch, "E86", {"center": v(0, 120) * mm, "radius": 6 * mm});
            skLineSegment(sketch, "E87", {"start": v(-80, 0) * mm, "end": v(80, 0) * mm, "construction": true});
            skCircle(sketch, "E88.MirrorC", {"center": v(0, -120) * mm, "radius": 6 * mm});
            skLineSegment(sketch, "E89.MirrorCS", {"start": v(15, -108) * mm, "end": v(33, -90) * mm});
            skLineSegment(sketch, "E90.MirrorCS", {"start": v(0, -90) * mm, "end": v(0, -120) * mm, "construction": true});
            skLineSegment(sketch, "E91.MirrorCS", {"start": v(-33, -90) * mm, "end": v(-15, -108) * mm});
            skLineSegment(sketch, "E92.MirrorCS", {"start": v(-15, -108) * mm, "end": v(-15, -120) * mm});
            skArc(sketch, "E93.MirrorCS", {"start": v(15, -120) * mm, "mid": v(0, -135) * mm, "end": v(-15, -120) * mm});
            skLineSegment(sketch, "E94.MirrorCS", {"start": v(15, -120) * mm, "end": v(15, -108) * mm});
            skArc(sketch, "E95.0", {"start": v(-56.15, -48.18) * mm, "mid": v(0, -67.5) * mm, "end": v(56.15, -48.18) * mm});
            skArc(sketch, "E95.1", {"start": v(56.15, -48.18) * mm, "mid": v(58.99, -44.68) * mm, "end": v(60, -40.3) * mm});
            skLineSegment(sketch, "E95.2", {"start": v(60, 40.3) * mm, "end": v(60, -40.3) * mm});
            skPoint(sketch, "E95.3", {"position": v(60, 40.3) * mm});
            skArc(sketch, "E95.4", {"start": v(60, 40.3) * mm, "mid": v(58.99, 44.68) * mm, "end": v(56.15, 48.18) * mm});
            skArc(sketch, "E95.5", {"start": v(56.15, 48.18) * mm, "mid": v(0, 67.5) * mm, "end": v(-56.15, 48.18) * mm});
            skArc(sketch, "E95.6", {"start": v(-56.15, 48.18) * mm, "mid": v(-58.99, 44.68) * mm, "end": v(-60, 40.3) * mm});
            skLineSegment(sketch, "E95.7", {"start": v(-60, 40.3) * mm, "end": v(-60, -40.3) * mm});
            skArc(sketch, "E95.8", {"start": v(-60, -40.3) * mm, "mid": v(-58.99, -44.68) * mm, "end": v(-56.15, -48.18) * mm});
            skSolve(sketch);
        }
        {
            var Q0;
            Q0 = qSketchRegion(id + "F16", true);
            var Q1;
            Q1=makeQuery(id+"F2.opExtrude","CAP_FACE",FACE,{"disambiguationData":[OSD([sQuery(id+"F0.wireOp",EDGE,"E12"),sQuery(id+"F0.wireOp",EDGE,"E13"),sQuery(id+"F0.wireOp",EDGE,"E14"),sQuery(id+"F0.wireOp",EDGE,"E15"),sQuery(id+"F0.wireOp",EDGE,"E17.filletArc"),sQuery(id+"F0.wireOp",EDGE,"E18.filletArc"),sQuery(id+"F0.wireOp",EDGE,"E19.filletArc"),sQuery(id+"F0.wireOp",EDGE,"E20.filletArc"),sQuery(id+"F0.wireOp",EDGE,"E25.0"),sQuery(id+"F0.wireOp",EDGE,"E25.1"),sQuery(id+"F0.wireOp",EDGE,"E25.2"),sQuery(id+"F0.wireOp",EDGE,"E25.3"),sQuery(id+"F0.wireOp",EDGE,"E25.4"),sQuery(id+"F0.wireOp",EDGE,"E25.5"),sQuery(id+"F0.wireOp",EDGE,"E25.6"),sQuery(id+"F0.wireOp",EDGE,"E25.7")])],"isStart":false});
            extrude(context, id + "F17", {"entities" : qUnion([Q0]), "endBound" : BoundingType.UP_TO_SURFACE, "endBoundEntityFace" : qUnion([Q1]), "depth" : 25 * mm});
        }
    });
